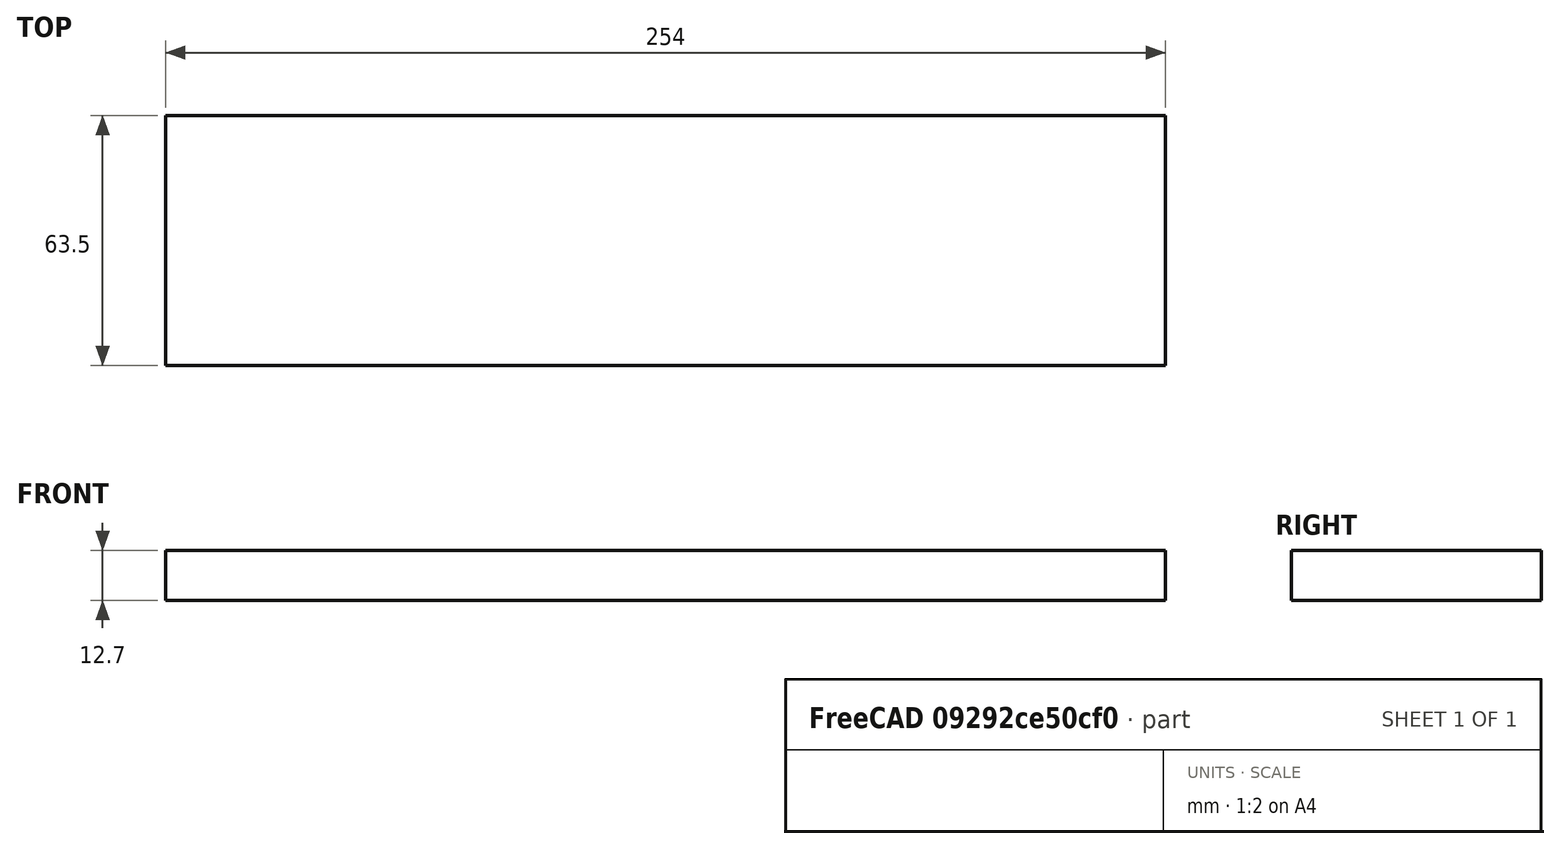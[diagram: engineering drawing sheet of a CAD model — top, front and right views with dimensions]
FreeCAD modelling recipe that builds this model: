
FCSTD DOCUMENT  (FreeCAD 0.16R6702 (Git))
Label: trackpadbasic
License: All rights reserved
LicenseURL: http://en.wikipedia.org/wiki/All_rights_reserved
objects: Sketcher::SketchObject×1, PartDesign::Pad×1
note: 3 computed .brp shape members not serialized (recipe doc carries the construction recipe); baked Part::Feature solids carry a one-line shape summary decoded from their .brp

FEATURE [Sketcher::SketchObject] Sketch
  sketch-geometry (4):
    g0: LineSegment StartX=-127 StartY=60.6716 StartZ=0 EndX=127 EndY=60.6716 EndZ=0
    g1: LineSegment StartX=127 StartY=60.6716 StartZ=0 EndX=127 EndY=-2.82843 EndZ=0
    g2: LineSegment StartX=127 StartY=-2.82843 StartZ=0 EndX=-127 EndY=-2.82843 EndZ=0
    g3: LineSegment StartX=-127 StartY=-2.82843 StartZ=0 EndX=-127 EndY=60.6716 EndZ=0
  constraints (10):
    c: Coincident(g0,g1)
    c: Coincident(g1,g2)
    c: Coincident(g2,g3)
    c: Coincident(g3,g0)
    c: Horizontal(g0)
    c: Horizontal(g2)
    c: Vertical(g1)
    c: Vertical(g3)
    c: DistanceX(g0,g0) = 254
    c: DistanceY(g3,g3) = 63.5
FEATURE [PartDesign::Pad] Pad
  Length = 12.7
  Length2 = 100
  Sketch = -> Sketch
  Type = 0
